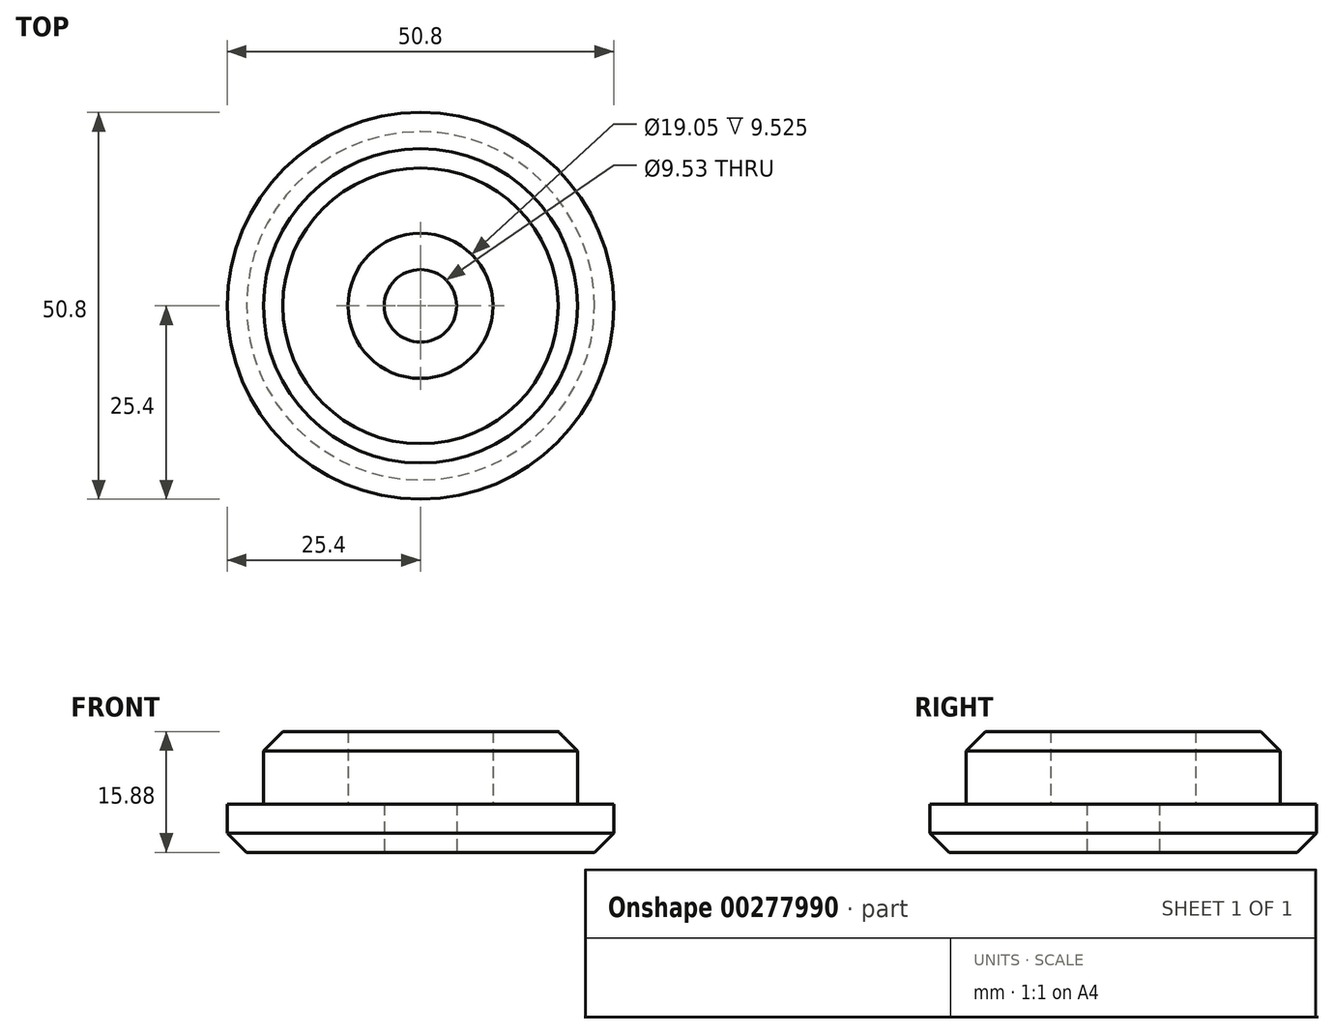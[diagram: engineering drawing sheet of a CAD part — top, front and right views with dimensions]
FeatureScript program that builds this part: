
annotation { "Feature Type Name" : "Feature", "Feature Type Description" : "" }
export const myFeature = defineFeature(function(context is Context, id is Id, definition is map)
    precondition{}
    {
        {
            var Q0;
            Q0=qCreatedBy(makeId("Front.planeOp"),FACE);
            var sketch = newSketch(context, id + "F0", { "sketchPlane" : qUnion([Q0])});
            skLineSegment(sketch, "E0", {"start": v(25.4, 0) * mm, "end": v(25.4, 6.35) * mm});
            skLineSegment(sketch, "E1", {"start": v(25.4, 6.35) * mm, "end": v(20.64, 6.35) * mm});
            skLineSegment(sketch, "E2", {"start": v(20.64, 6.35) * mm, "end": v(20.64, 15.88) * mm});
            skLineSegment(sketch, "E3", {"start": v(20.64, 15.88) * mm, "end": v(9.53, 15.88) * mm});
            skLineSegment(sketch, "E4", {"start": v(9.53, 15.88) * mm, "end": v(9.53, 6.35) * mm});
            skLineSegment(sketch, "E5", {"start": v(0, 0) * mm, "end": v(0, 33.78) * mm, "construction": true});
            skLineSegment(sketch, "E6", {"start": v(9.53, 6.35) * mm, "end": v(4.76, 6.35) * mm});
            skLineSegment(sketch, "E7", {"start": v(4.76, 6.35) * mm, "end": v(4.76, 0) * mm});
            skLineSegment(sketch, "E8", {"start": v(4.76, 0) * mm, "end": v(25.4, 0) * mm});
            skSolve(sketch);
        }
        {
            var Q0;
            Q0=makeQuery(id+"F0.imprint","IMPRINT",FACE,{"disambiguationData":[TD([[makeQuery(id+"F0.imprint","IMPRINT",EDGE,{"derivedFrom":sQuery(id+"F0.wireOp",EDGE,"E0")}),1.0]])]});
            var Q1;
            Q1=sQuery(id+"F0.wireOp",EDGE,"E5");
            revolve(context, id + "F1", {"entities" : qUnion([Q0]), "axis" : qUnion([Q1]), "revolveType" : RevolveType.FULL});
        }
        {
            var Q0;
            Q0=makeQuery(id+"F1.opRevolve","SWEPT_EDGE",EDGE,{"disambiguationData":[OSD([sQuery(id+"F0.wireOp",EDGE,"E2"),sQuery(id+"F0.wireOp",EDGE,"E3")])]});
            var Q1;
            Q1=makeQuery(id+"F1.opRevolve","SWEPT_EDGE",EDGE,{"disambiguationData":[OSD([sQuery(id+"F0.wireOp",EDGE,"E0"),sQuery(id+"F0.wireOp",EDGE,"E8")])]});
            chamfer(context, id + "F2", {"entities" : qUnion([Q0, Q1]), "chamferType" : ChamferType.OFFSET_ANGLE, "width" : 2.54 * mm, "oppositeDirection" : false, "angle" : 45 * degree, "tangentPropagation" : true});
        }
    });
